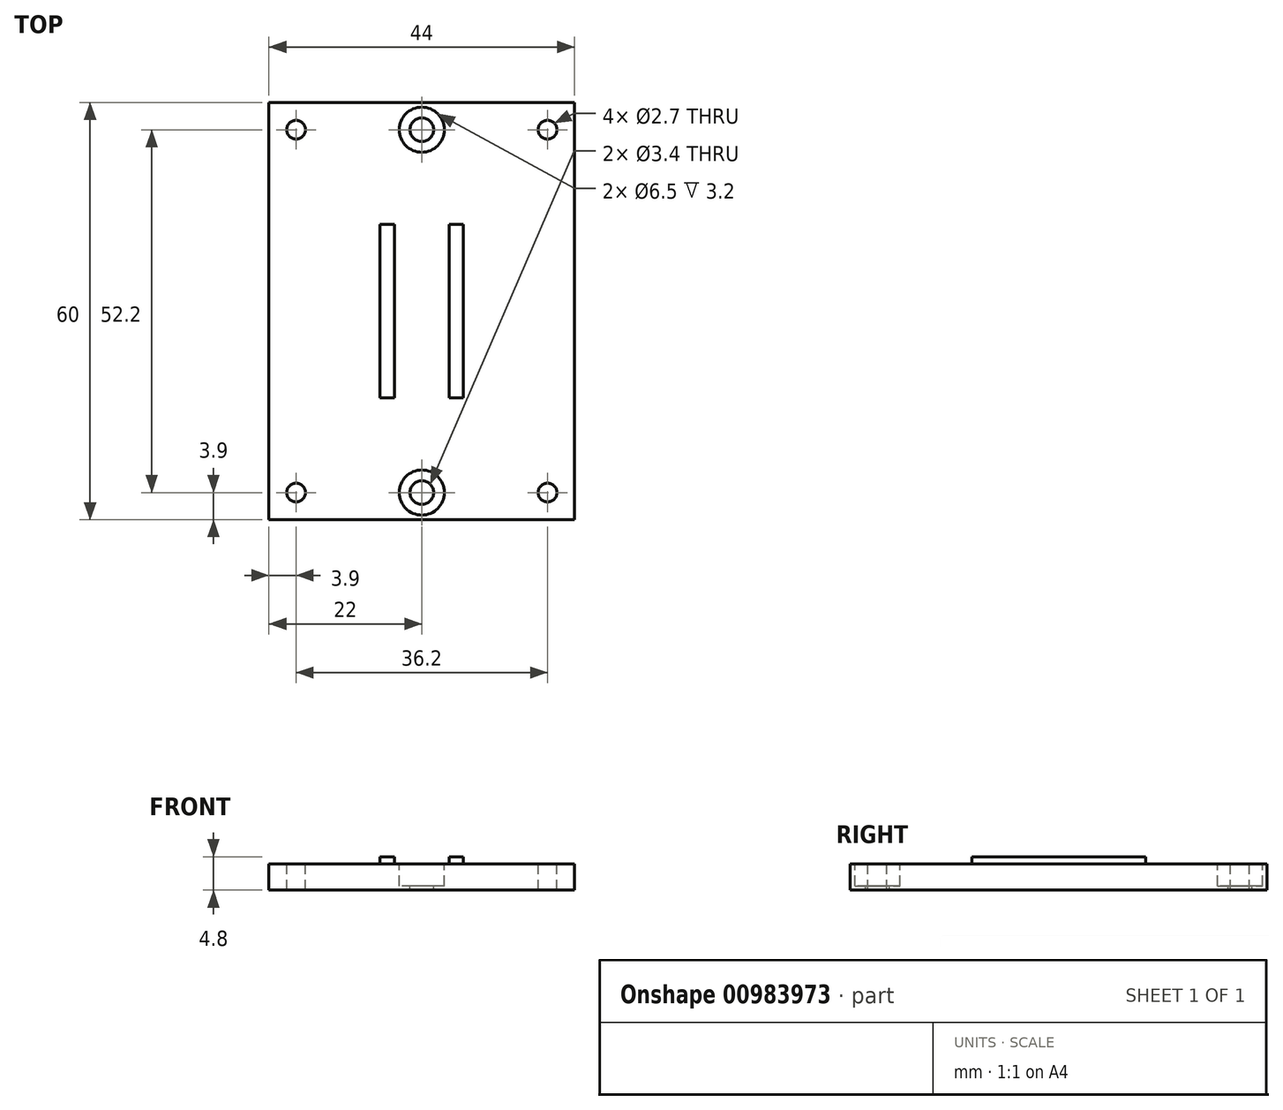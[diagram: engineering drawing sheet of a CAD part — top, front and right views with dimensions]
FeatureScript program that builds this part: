
annotation { "Feature Type Name" : "Feature", "Feature Type Description" : "" }
export const myFeature = defineFeature(function(context is Context, id is Id, definition is map)
    precondition{}
    {
        {
            var Q0;
            Q0=qCreatedBy(makeId("Top.planeOp"),FACE);
            var sketch = newSketch(context, id + "F0", { "sketchPlane" : qUnion([Q0])});
            skLineSegment(sketch, "E0.bottom", {"start": v(-22, 30) * mm, "end": v(22, 30) * mm});
            skLineSegment(sketch, "E0.top", {"start": v(-22, -30) * mm, "end": v(22, -30) * mm});
            skLineSegment(sketch, "E0.left", {"start": v(-22, 30) * mm, "end": v(-22, -30) * mm});
            skLineSegment(sketch, "E0.right", {"start": v(22, 30) * mm, "end": v(22, -30) * mm});
            skLineSegment(sketch, "E1", {"start": v(-89.67, 0) * mm, "end": v(97.44, 0) * mm, "construction": true});
            skLineSegment(sketch, "E2", {"start": v(0, 56.67) * mm, "end": v(0, -54.67) * mm, "construction": true});
            skSolve(sketch);
        }
        {
            var Q0;
            Q0 = qSketchRegion(id + "F0", true);
            extrude(context, id + "F1", {"entities" : qUnion([Q0]), "depth" : 3.8 * mm, "offsetDistance" : 25 * mm});
        }
        {
            var Q0;
            Q0=makeQuery(id+"F1.opExtrude","CAP_FACE",FACE,{"disambiguationData":[OSD([sQuery(id+"F0.wireOp",EDGE,"E0.bottom"),sQuery(id+"F0.wireOp",EDGE,"E0.top"),sQuery(id+"F0.wireOp",EDGE,"E0.left"),sQuery(id+"F0.wireOp",EDGE,"E0.right")])],"isStart":false});
            var sketch = newSketch(context, id + "F2", { "sketchPlane" : qUnion([Q0])});
            skPoint(sketch, "E3", {"position": v(18.1, -26.1) * mm});
            skPoint(sketch, "E4", {"position": v(18.1, 26.1) * mm});
            skPoint(sketch, "E5", {"position": v(-18.1, 26.1) * mm});
            skPoint(sketch, "E6", {"position": v(-18.1, -26.1) * mm});
            skPoint(sketch, "E7", {"position": v(0, 26.1) * mm});
            skPoint(sketch, "E8", {"position": v(0, -26.1) * mm});
            skSolve(sketch);
        }
        {
            var Q0;
            Q0=sQuery(id+"F2.wireOp",VERTEX,"E5");
            var Q1;
            Q1=sQuery(id+"F2.wireOp",VERTEX,"E4");
            var Q2;
            Q2=sQuery(id+"F2.wireOp",VERTEX,"E3");
            var Q3;
            Q3=sQuery(id+"F2.wireOp",VERTEX,"E6");
            var Q4;
            Q4=makeQuery(id+"F1.opExtrude","SWEPT_BODY",BODY,{"disambiguationData":[OSD([sQuery(id+"F0.wireOp",EDGE,"E0.bottom"),sQuery(id+"F0.wireOp",EDGE,"E0.top"),sQuery(id+"F0.wireOp",EDGE,"E0.left"),sQuery(id+"F0.wireOp",EDGE,"E0.right")])]});
            hole(context, id + "F3", {"style" : HoleStyle.SIMPLE, "endStyle" : HoleEndStyle.THROUGH, "standardTappedOrClearance" : lookupTablePath({ "standard" : "ISO", "engagement" : "50%", "pitch" : "0.5 mm", "size" : "M3", "type" : "Tapped" }), "standardBlindInLast" : lookupTablePath({ "standard" : "ISO", "fit" : "Normal", "engagement" : "50%", "pitch" : "0.5 mm", "size" : "M3", "type" : "Clearance & tapped" }), "holeDiameter" : 2.7 * mm, "majorDiameter" : 3 * mm, "showTappedDepth" : true, "isTappedThrough" : true, "tappedDepth" : 8 * mm, "tapClearance" : 3, "locations" : qUnion([Q0, Q1, Q2, Q3]), "scope" : qUnion([Q4])});
        }
        {
            var Q0;
            Q0=sQuery(id+"F2.wireOp",VERTEX,"E7");
            var Q1;
            Q1=sQuery(id+"F2.wireOp",VERTEX,"E8");
            var Q2;
            Q2=makeQuery(id+"F1.opExtrude","SWEPT_BODY",BODY,{"disambiguationData":[OSD([sQuery(id+"F0.wireOp",EDGE,"E0.bottom"),sQuery(id+"F0.wireOp",EDGE,"E0.top"),sQuery(id+"F0.wireOp",EDGE,"E0.left"),sQuery(id+"F0.wireOp",EDGE,"E0.right")])]});
            hole(context, id + "F4", {"style" : HoleStyle.C_BORE, "endStyle" : HoleEndStyle.THROUGH, "holeDiameter" : 3.4 * mm, "cBoreDiameter" : 6.5 * mm, "cBoreDepth" : 3.2 * mm, "majorDiameter" : 5 * mm, "isTappedThrough" : true, "tappedDepth" : 8 * mm, "tapClearance" : 3, "startFromSketch" : true, "locations" : qUnion([Q0, Q1]), "scope" : qUnion([Q2])});
        }
        {
            var Q0;
            Q0=makeQuery(id+"F1.opExtrude","CAP_FACE",FACE,{"disambiguationData":[OSD([sQuery(id+"F0.wireOp",EDGE,"E0.bottom"),sQuery(id+"F0.wireOp",EDGE,"E0.top"),sQuery(id+"F0.wireOp",EDGE,"E0.left"),sQuery(id+"F0.wireOp",EDGE,"E0.right")])],"isStart":false});
            var sketch = newSketch(context, id + "F5", { "sketchPlane" : qUnion([Q0])});
            skLineSegment(sketch, "E9.bottom", {"start": v(-6, 12.5) * mm, "end": v(-3.95, 12.5) * mm});
            skLineSegment(sketch, "E9.top", {"start": v(-6, -12.5) * mm, "end": v(-3.95, -12.5) * mm});
            skLineSegment(sketch, "E9.left", {"start": v(-6, 12.5) * mm, "end": v(-6, -12.5) * mm});
            skLineSegment(sketch, "E9.right", {"start": v(-3.95, 12.5) * mm, "end": v(-3.95, -12.5) * mm});
            skLineSegment(sketch, "E10.bottom", {"start": v(3.95, 12.5) * mm, "end": v(6, 12.5) * mm});
            skLineSegment(sketch, "E10.top", {"start": v(3.95, -12.5) * mm, "end": v(6, -12.5) * mm});
            skLineSegment(sketch, "E10.left", {"start": v(3.95, 12.5) * mm, "end": v(3.95, -12.5) * mm});
            skLineSegment(sketch, "E10.right", {"start": v(6, 12.5) * mm, "end": v(6, -12.5) * mm});
            skSolve(sketch);
        }
        {
            var Q0;
            Q0 = qSketchRegion(id + "F5", true);
            extrude(context, id + "F6", {"entities" : qUnion([Q0]), "operationType" : NewBodyOperationType.ADD, "depth" : 1 * mm, "offsetDistance" : 25 * mm});
        }
    });
